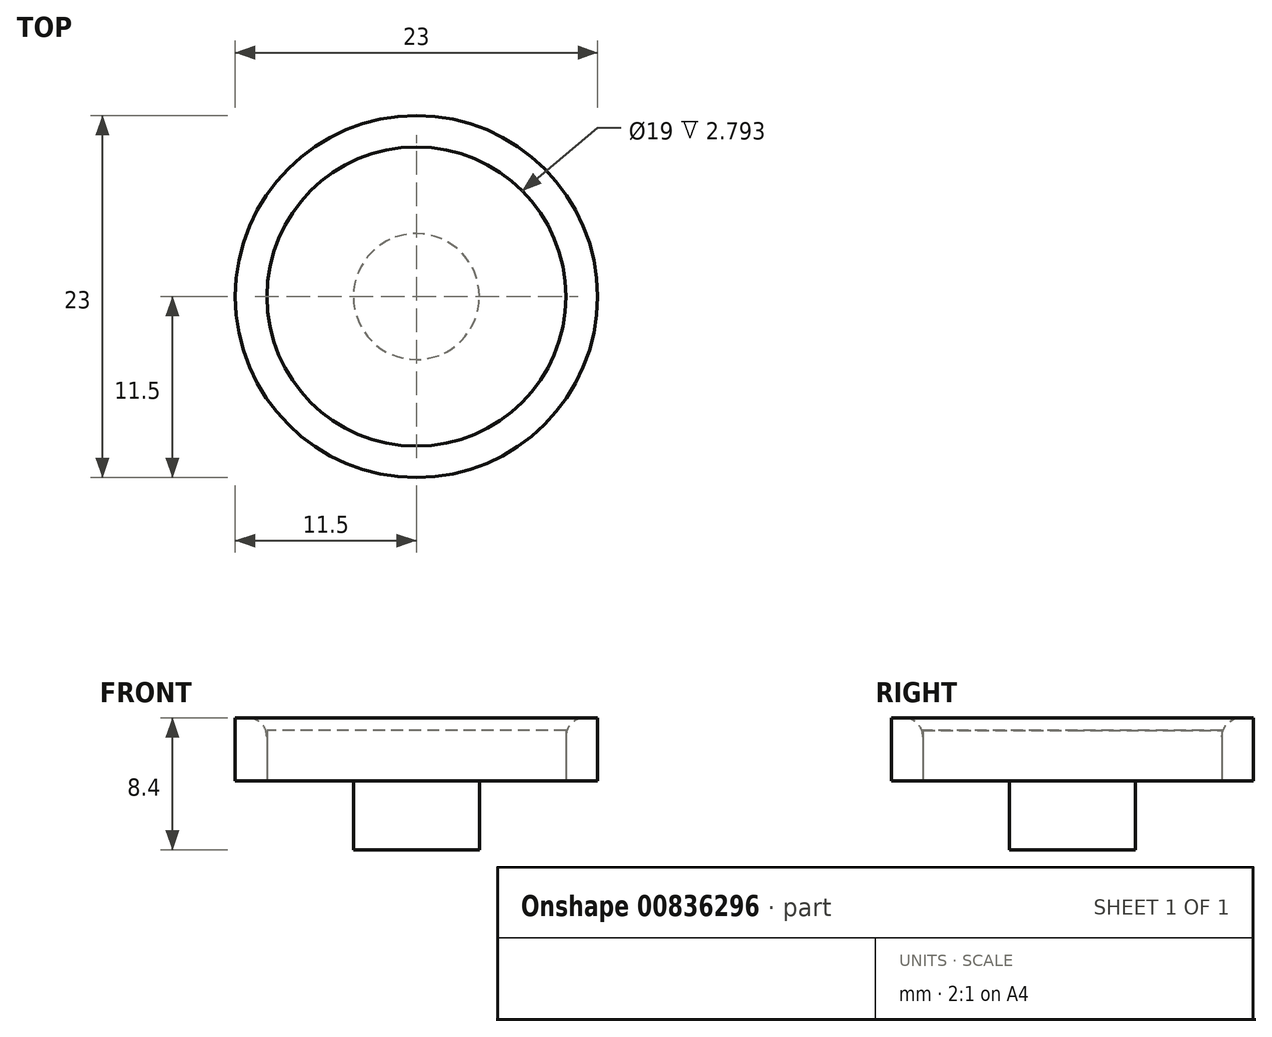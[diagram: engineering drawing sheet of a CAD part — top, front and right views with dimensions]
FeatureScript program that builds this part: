
annotation { "Feature Type Name" : "Feature", "Feature Type Description" : "" }
export const myFeature = defineFeature(function(context is Context, id is Id, definition is map)
    precondition{}
    {
        {
            var Q0;
            Q0=qCreatedBy(makeId("Top.planeOp"),FACE);
            var sketch = newSketch(context, id + "F0", { "sketchPlane" : qUnion([Q0])});
            skCircle(sketch, "E0", {"center": v(0, 0) * mm, "radius": 11.5 * mm});
            skCircle(sketch, "E1", {"center": v(0, 0) * mm, "radius": 9.5 * mm});
            skSolve(sketch);
        }
        {
            var Q0;
            Q0=makeQuery(id+"F0.imprint","IMPRINT",FACE,{"disambiguationData":[TD([[makeQuery(id+"F0.imprint","IMPRINT",EDGE,{"derivedFrom":sQuery(id+"F0.wireOp",EDGE,"E0")}),1.0]])]});
            extrude(context, id + "F1", {"entities" : qUnion([Q0]), "depth" : 4 * mm, "offsetDistance" : 25 * mm});
        }
        {
            var Q0;
            Q0=makeQuery(id+"F0.imprint","IMPRINT",FACE,{"disambiguationData":[TD([[makeQuery(id+"F0.imprint","IMPRINT",EDGE,{"derivedFrom":sQuery(id+"F0.wireOp",EDGE,"E1")}),1.0]])]});
            extrude(context, id + "F2", {"entities" : qUnion([Q0]), "depth" : 3.2 * mm, "offsetDistance" : 25 * mm});
        }
        {
            var Q0;
            Q0=makeQuery(id+"F1.opExtrude","CAP_EDGE",EDGE,{"disambiguationData":[OSD([sQuery(id+"F0.wireOp",EDGE,"E1")])],"isStart":false});
            fillet(context, id + "F3", {"entities" : qUnion([Q0]), "radius" : 1.2 * mm, "tangentPropagation" : true, "allowEdgeOverflow" : false});
        }
        {
            var Q0;
            Q0=qCreatedBy(makeId("Top.planeOp"),FACE);
            var sketch = newSketch(context, id + "F4", { "sketchPlane" : qUnion([Q0])});
            skCircle(sketch, "E2", {"center": v(0, 0) * mm, "radius": 4 * mm});
            skSolve(sketch);
        }
        {
            var Q0;
            Q0=makeQuery(id+"F4.imprint","IMPRINT",FACE,{"disambiguationData":[TD([[makeQuery(id+"F4.imprint","IMPRINT",EDGE,{"derivedFrom":sQuery(id+"F4.wireOp",EDGE,"E2")}),1.0]])]});
            extrude(context, id + "F5", {"entities" : qUnion([Q0]), "operationType" : NewBodyOperationType.ADD, "oppositeDirection" : true, "depth" : 4.4 * mm, "offsetDistance" : 25 * mm});
        }
    });
